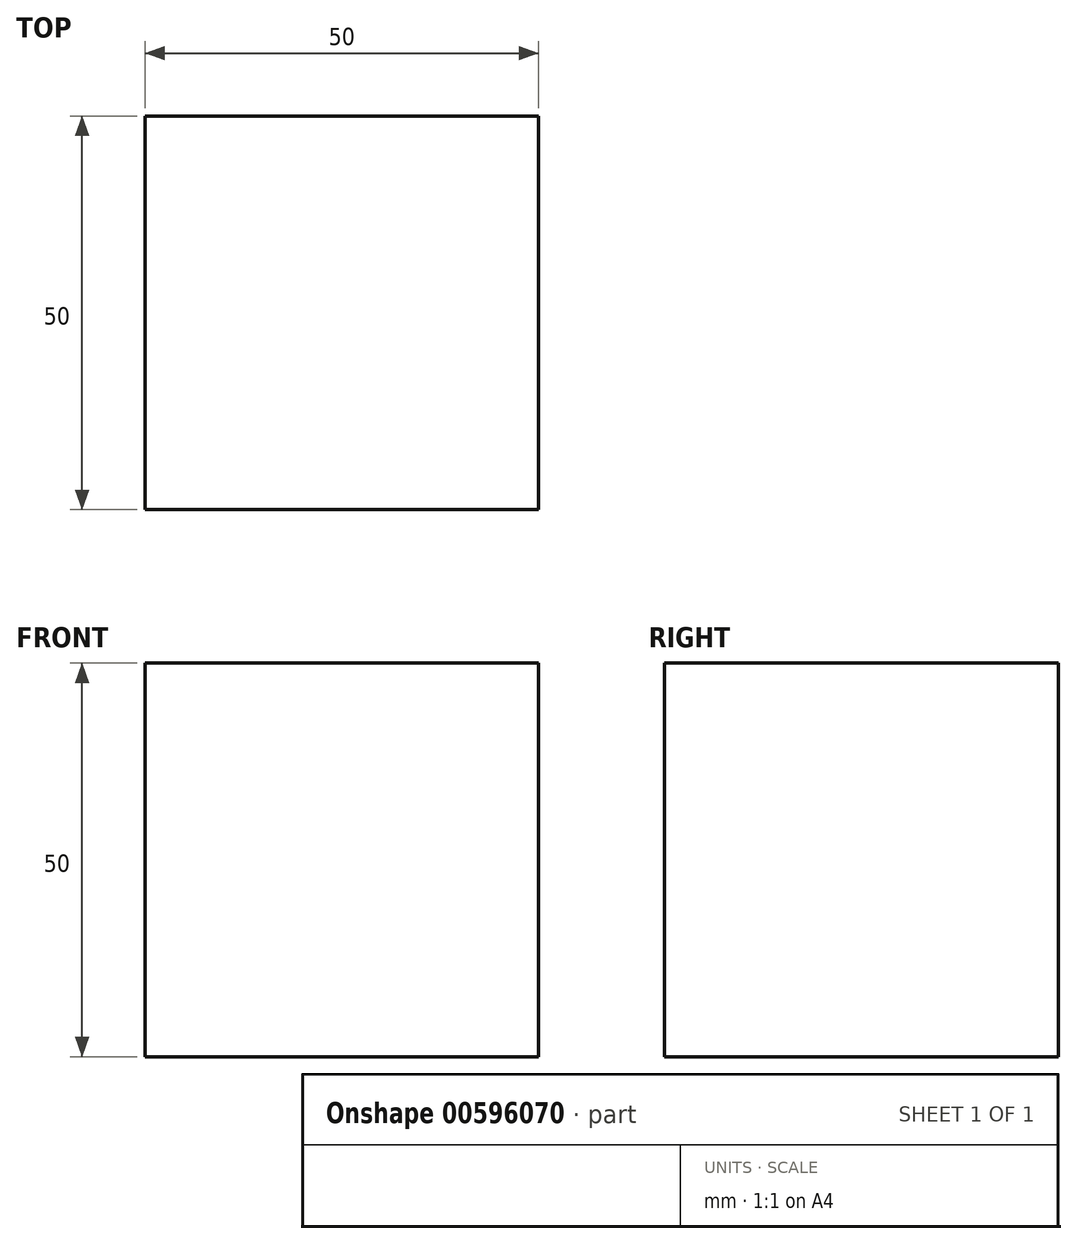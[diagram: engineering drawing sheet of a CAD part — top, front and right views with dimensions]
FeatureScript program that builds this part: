
annotation { "Feature Type Name" : "Feature", "Feature Type Description" : "" }
export const myFeature = defineFeature(function(context is Context, id is Id, definition is map)
    precondition{}
    {
        {
            var Q0;
            Q0=qCreatedBy(makeId("Top.planeOp"),FACE);
            var sketch = newSketch(context, id + "F0", { "sketchPlane" : qUnion([Q0])});
            skLineSegment(sketch, "E0.bottom", {"start": v(-25, 25) * mm, "end": v(25, 25) * mm});
            skLineSegment(sketch, "E0.top", {"start": v(-25, -25) * mm, "end": v(25, -25) * mm});
            skLineSegment(sketch, "E0.left", {"start": v(-25, 25) * mm, "end": v(-25, -25) * mm});
            skLineSegment(sketch, "E0.right", {"start": v(25, 25) * mm, "end": v(25, -25) * mm});
            skPoint(sketch, "E0.middle", {"position": v(0, 0) * mm});
            skSolve(sketch);
        }
        {
            var Q0;
            Q0 = qSketchRegion(id + "F0", true);
            extrude(context, id + "F1", {"entities" : qUnion([Q0]), "depth" : 50 * mm, "offsetDistance" : 25 * mm});
        }
    });
